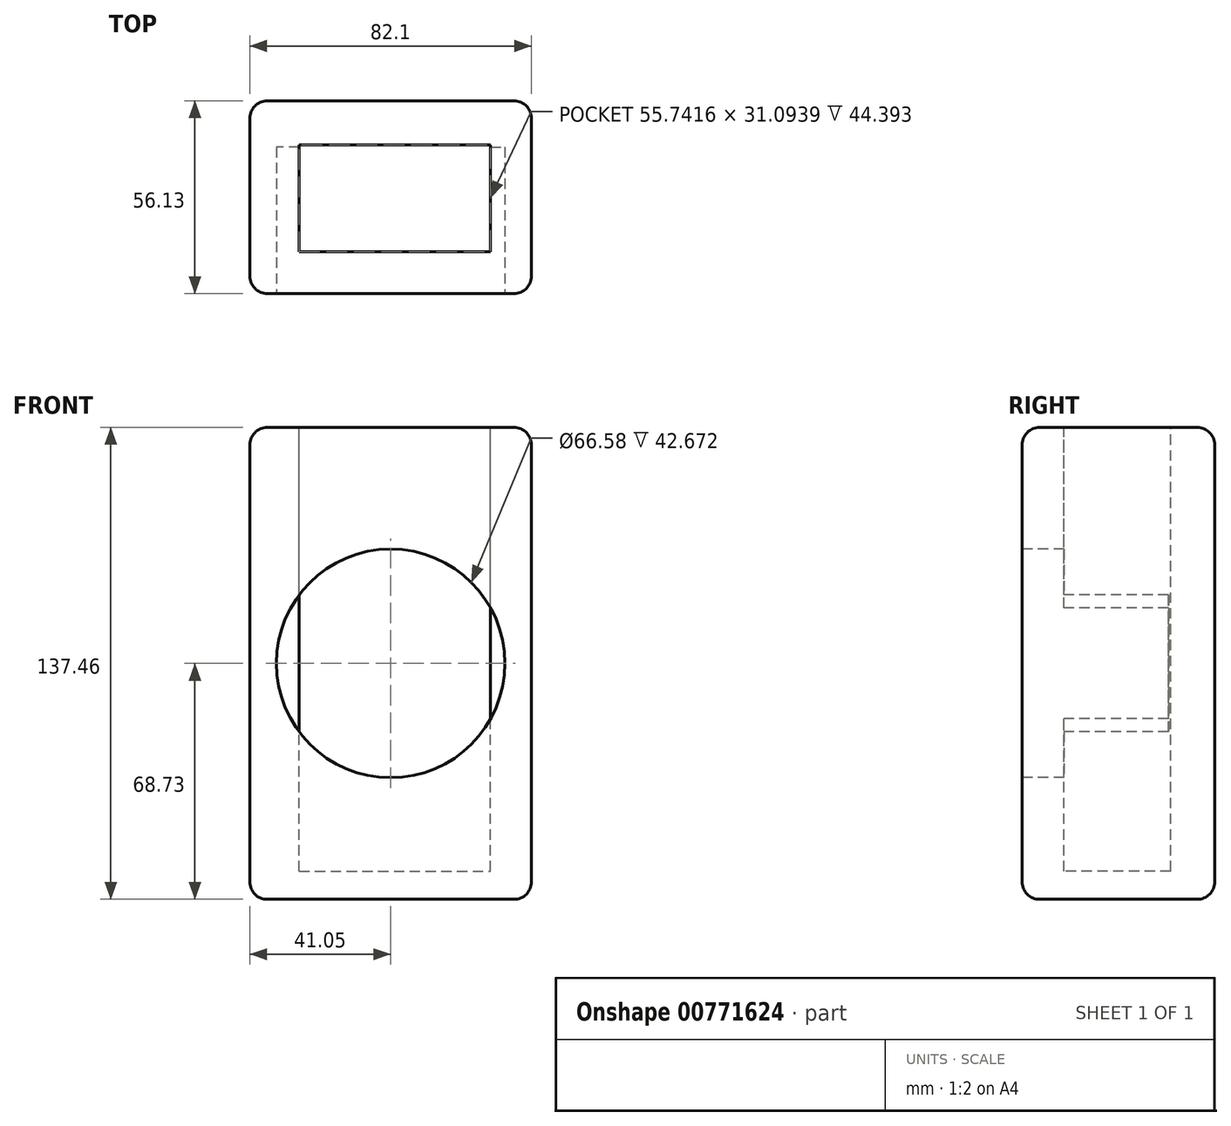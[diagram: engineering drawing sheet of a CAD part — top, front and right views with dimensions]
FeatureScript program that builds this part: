
annotation { "Feature Type Name" : "Feature", "Feature Type Description" : "" }
export const myFeature = defineFeature(function(context is Context, id is Id, definition is map)
    precondition{}
    {
        {
            var Q0;
            Q0=qCreatedBy(makeId("Front.planeOp"),FACE);
            var sketch = newSketch(context, id + "F0", { "sketchPlane" : qUnion([Q0])});
            skLineSegment(sketch, "E0.bottom", {"start": v(41.05, -68.73) * mm, "end": v(-41.05, -68.73) * mm});
            skLineSegment(sketch, "E0.top", {"start": v(41.05, 68.73) * mm, "end": v(-41.05, 68.73) * mm});
            skLineSegment(sketch, "E0.left", {"start": v(41.05, -68.73) * mm, "end": v(41.05, 68.73) * mm});
            skLineSegment(sketch, "E0.right", {"start": v(-41.05, -68.73) * mm, "end": v(-41.05, 68.73) * mm});
            skPoint(sketch, "E0.middle", {"position": v(0, 0) * mm});
            skSolve(sketch);
        }
        {
            var Q0;
            Q0 = qSketchRegion(id + "F0", true);
            extrude(context, id + "F1", {"entities" : qUnion([Q0]), "depth" : 56.13 * mm, "offsetDistance" : 25.4 * mm});
        }
        {
            var Q0;
            Q0=makeQuery(id+"F1.opExtrude","CAP_EDGE",EDGE,{"disambiguationData":[OSD([sQuery(id+"F0.wireOp",EDGE,"E0.top")])],"isStart":false});
            var Q1;
            Q1=makeQuery(id+"F1.opExtrude","SWEPT_EDGE",EDGE,{"disambiguationData":[OSD([sQuery(id+"F0.wireOp",EDGE,"E0.top"),sQuery(id+"F0.wireOp",EDGE,"E0.left")])]});
            var Q2;
            Q2=makeQuery(id+"F1.opExtrude","CAP_EDGE",EDGE,{"disambiguationData":[OSD([sQuery(id+"F0.wireOp",EDGE,"E0.top")])],"isStart":true});
            var Q3;
            Q3=makeQuery(id+"F1.opExtrude","SWEPT_EDGE",EDGE,{"disambiguationData":[OSD([sQuery(id+"F0.wireOp",EDGE,"E0.top"),sQuery(id+"F0.wireOp",EDGE,"E0.right")])]});
            var Q4;
            Q4=makeQuery(id+"F1.opExtrude","CAP_EDGE",EDGE,{"disambiguationData":[OSD([sQuery(id+"F0.wireOp",EDGE,"E0.left")])],"isStart":false});
            var Q5;
            Q5=makeQuery(id+"F1.opExtrude","CAP_EDGE",EDGE,{"disambiguationData":[OSD([sQuery(id+"F0.wireOp",EDGE,"E0.right")])],"isStart":false});
            var Q6;
            Q6=makeQuery(id+"F1.opExtrude","CAP_EDGE",EDGE,{"disambiguationData":[OSD([sQuery(id+"F0.wireOp",EDGE,"E0.bottom")])],"isStart":false});
            var Q7;
            Q7=makeQuery(id+"F1.opExtrude","SWEPT_EDGE",EDGE,{"disambiguationData":[OSD([sQuery(id+"F0.wireOp",EDGE,"E0.bottom"),sQuery(id+"F0.wireOp",EDGE,"E0.left")])]});
            var Q8;
            Q8=makeQuery(id+"F1.opExtrude","CAP_EDGE",EDGE,{"disambiguationData":[OSD([sQuery(id+"F0.wireOp",EDGE,"E0.bottom")])],"isStart":true});
            var Q9;
            Q9=makeQuery(id+"F1.opExtrude","SWEPT_EDGE",EDGE,{"disambiguationData":[OSD([sQuery(id+"F0.wireOp",EDGE,"E0.bottom"),sQuery(id+"F0.wireOp",EDGE,"E0.right")])]});
            var Q10;
            Q10=makeQuery(id+"F1.opExtrude","CAP_EDGE",EDGE,{"disambiguationData":[OSD([sQuery(id+"F0.wireOp",EDGE,"E0.left")])],"isStart":true});
            var Q11;
            Q11=makeQuery(id+"F1.opExtrude","CAP_EDGE",EDGE,{"disambiguationData":[OSD([sQuery(id+"F0.wireOp",EDGE,"E0.right")])],"isStart":true});
            fillet(context, id + "F2", {"entities" : qUnion([Q0, Q1, Q2, Q3, Q4, Q5, Q6, Q7, Q8, Q9, Q10, Q11]), "radius" : 5.08 * mm, "tangentPropagation" : true, "allowEdgeOverflow" : false});
        }
        {
            var Q0;
            Q0=makeQuery(id+"F1.opExtrude","SWEPT_FACE",FACE,{"disambiguationData":[OSD([sQuery(id+"F0.wireOp",EDGE,"E0.top")])]});
            var sketch = newSketch(context, id + "F3", { "sketchPlane" : qUnion([Q0])});
            skLineSegment(sketch, "E1", {"start": v(-26.64, -12.8) * mm, "end": v(29.1, -12.8) * mm});
            skLineSegment(sketch, "E2", {"start": v(-26.64, -12.8) * mm, "end": v(-26.64, -43.9) * mm});
            skLineSegment(sketch, "E3", {"start": v(-26.64, -43.9) * mm, "end": v(29.1, -43.9) * mm});
            skLineSegment(sketch, "E4", {"start": v(29.1, -43.9) * mm, "end": v(29.1, -12.8) * mm});
            skSolve(sketch);
        }
        {
            var Q0;
            Q0=makeQuery(id+"F1.opExtrude","CAP_FACE",FACE,{"disambiguationData":[OSD([sQuery(id+"F0.wireOp",EDGE,"E0.bottom"),sQuery(id+"F0.wireOp",EDGE,"E0.top"),sQuery(id+"F0.wireOp",EDGE,"E0.left"),sQuery(id+"F0.wireOp",EDGE,"E0.right")])],"isStart":false});
            var sketch = newSketch(context, id + "F4", { "sketchPlane" : qUnion([Q0])});
            skCircle(sketch, "E5", {"center": v(0, 0) * mm, "radius": 33.3 * mm});
            skSolve(sketch);
        }
        {
            var Q0;
            Q0=makeQuery(id+"F3.imprint","IMPRINT",FACE,{"disambiguationData":[TD([[makeQuery(id+"F3.imprint","IMPRINT",EDGE,{"derivedFrom":sQuery(id+"F3.wireOp",EDGE,"E1")}),-1.0]])]});
            extrude(context, id + "F5", {"entities" : qUnion([Q0]), "operationType" : NewBodyOperationType.REMOVE, "oppositeDirection" : true, "depth" : 129.29 * mm, "offsetDistance" : 25.4 * mm});
        }
        {
            var Q0;
            Q0=makeQuery(id+"F4.imprint","IMPRINT",FACE,{"disambiguationData":[TD([[makeQuery(id+"F4.imprint","IMPRINT",EDGE,{"derivedFrom":sQuery(id+"F4.wireOp",EDGE,"E5")}),1.0]])]});
            extrude(context, id + "F6", {"entities" : qUnion([Q0]), "operationType" : NewBodyOperationType.REMOVE, "oppositeDirection" : true, "depth" : 42.67 * mm, "offsetDistance" : 25.4 * mm});
        }
    });
